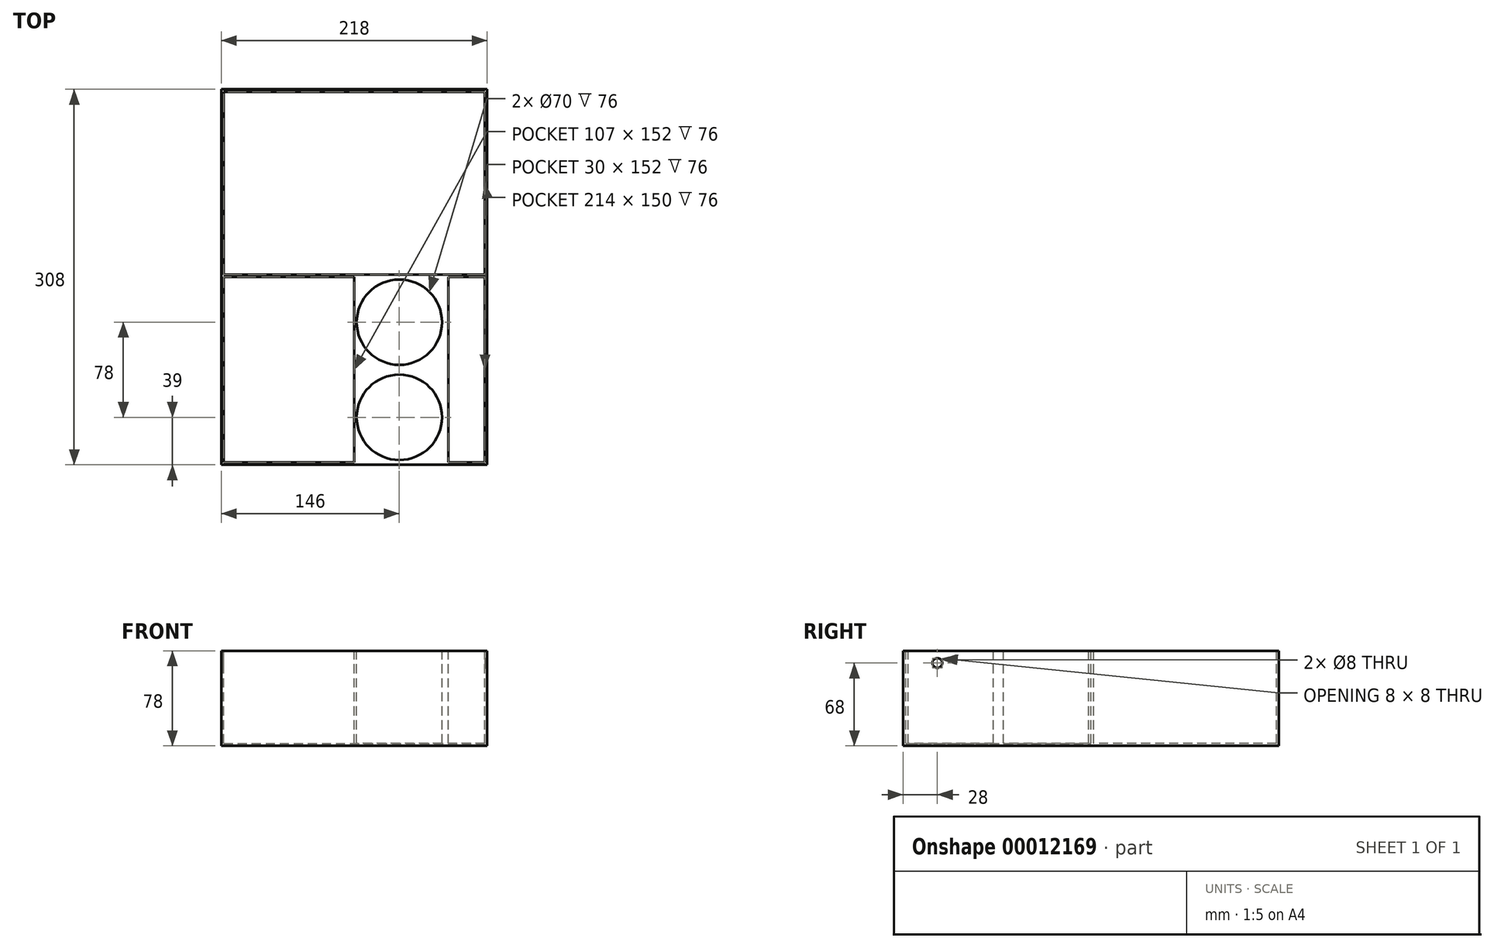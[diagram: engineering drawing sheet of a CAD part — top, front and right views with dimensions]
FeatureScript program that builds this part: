
annotation { "Feature Type Name" : "Feature", "Feature Type Description" : "" }
export const myFeature = defineFeature(function(context is Context, id is Id, definition is map)
    precondition{}
    {
        {
            var Q0;
            Q0=qCreatedBy(makeId("Top.planeOp"),FACE);
            var sketch = newSketch(context, id + "F0", { "sketchPlane" : qUnion([Q0])});
            skLineSegment(sketch, "E0.rect.bottom", {"start": v(109, 154) * mm, "end": v(-109, 154) * mm});
            skLineSegment(sketch, "E0.rect.top", {"start": v(109, -154) * mm, "end": v(-109, -154) * mm});
            skLineSegment(sketch, "E0.rect.left", {"start": v(109, 154) * mm, "end": v(109, -154) * mm});
            skLineSegment(sketch, "E0.rect.right", {"start": v(-109, 154) * mm, "end": v(-109, -154) * mm});
            skPoint(sketch, "E0.rect.middle", {"position": v(0, 0) * mm});
            skSolve(sketch);
        }
        {
            var Q0;
            Q0=makeQuery(id+"F0.imprint","IMPRINT",FACE,{"disambiguationData":[TD([[makeQuery(id+"F0.imprint","IMPRINT",EDGE,{"derivedFrom":sQuery(id+"F0.wireOp",EDGE,"E0.rect.bottom")}),1.0]])]});
            extrude(context, id + "F1", {"entities" : qUnion([Q0]), "depth" : 78 * mm});
        }
        {
            var Q0;
            Q0=makeQuery(id+"F1.opExtrude","CAP_FACE",FACE,{"disambiguationData":[OSD([sQuery(id+"F0.wireOp",EDGE,"E0.rect.bottom"),sQuery(id+"F0.wireOp",EDGE,"E0.rect.top"),sQuery(id+"F0.wireOp",EDGE,"E0.rect.left"),sQuery(id+"F0.wireOp",EDGE,"E0.rect.right")])],"isStart":false});
            var sketch = newSketch(context, id + "F2", { "sketchPlane" : qUnion([Q0])});
            skLineSegment(sketch, "E1", {"start": v(-109, 154) * mm, "end": v(-109, 152) * mm});
            skLineSegment(sketch, "E2", {"start": v(-109, 152) * mm, "end": v(-107, 152) * mm});
            skLineSegment(sketch, "E3", {"start": v(109, 154) * mm, "end": v(107, 154) * mm});
            skLineSegment(sketch, "E4", {"start": v(107, 154) * mm, "end": v(107, 152) * mm});
            skLineSegment(sketch, "E5.bottom", {"start": v(-107, 152) * mm, "end": v(107, 152) * mm});
            skLineSegment(sketch, "E5.top", {"start": v(-107, 2) * mm, "end": v(107, 2) * mm});
            skLineSegment(sketch, "E5.left", {"start": v(-107, 152) * mm, "end": v(-107, 2) * mm});
            skLineSegment(sketch, "E5.right", {"start": v(107, 152) * mm, "end": v(107, 2) * mm});
            skLineSegment(sketch, "E6", {"start": v(-107, 2) * mm, "end": v(-107, 0) * mm, "construction": true});
            skLineSegment(sketch, "E7", {"start": v(-109, -154) * mm, "end": v(-107, -154) * mm, "construction": true});
            skLineSegment(sketch, "E8", {"start": v(-107, -154) * mm, "end": v(-107, -152) * mm, "construction": true});
            skLineSegment(sketch, "E9.bottom", {"start": v(-107, -152) * mm, "end": v(0, -152) * mm});
            skLineSegment(sketch, "E9.top", {"start": v(-107, 0) * mm, "end": v(0, 0) * mm});
            skLineSegment(sketch, "E9.left", {"start": v(-107, -152) * mm, "end": v(-107, 0) * mm});
            skLineSegment(sketch, "E9.right", {"start": v(0, -152) * mm, "end": v(0, 0) * mm});
            skLineSegment(sketch, "E10", {"start": v(107, 2) * mm, "end": v(107, -154) * mm, "construction": true});
            skLineSegment(sketch, "E11", {"start": v(107, -154) * mm, "end": v(0, -154) * mm, "construction": true});
            skCircle(sketch, "E12", {"center": v(37, -115) * mm, "radius": 35 * mm});
            skCircle(sketch, "E13", {"center": v(37, -37) * mm, "radius": 35 * mm});
            skLineSegment(sketch, "E14", {"start": v(0, -37) * mm, "end": v(37, -37) * mm});
            skLineSegment(sketch, "E15", {"start": v(0, -115) * mm, "end": v(37, -115) * mm});
            skLineSegment(sketch, "E16.bottom", {"start": v(107, 0) * mm, "end": v(77, 0) * mm});
            skLineSegment(sketch, "E16.top", {"start": v(107, -152) * mm, "end": v(77, -152) * mm});
            skLineSegment(sketch, "E16.left", {"start": v(107, 0) * mm, "end": v(107, -152) * mm});
            skLineSegment(sketch, "E16.right", {"start": v(77, 0) * mm, "end": v(77, -152) * mm});
            skSolve(sketch);
        }
        {
            var Q0;
            Q0=makeQuery(id+"F2.imprint","IMPRINT",FACE,{"disambiguationData":[TD([[makeQuery(id+"F2.imprint","IMPRINT",EDGE,{"derivedFrom":sQuery(id+"F2.wireOp",EDGE,"E5.bottom")}),-1.0]])]});
            var Q1;
            Q1=makeQuery(id+"F2.imprint","IMPRINT",FACE,{"disambiguationData":[TD([[makeQuery(id+"F2.imprint","IMPRINT",EDGE,{"derivedFrom":sQuery(id+"F2.wireOp",EDGE,"E9.bottom")}),1.0]])]});
            var Q2;
            Q2=makeQuery(id+"F2.imprint","IMPRINT",FACE,{"disambiguationData":[TD([[makeQuery(id+"F2.imprint","IMPRINT",EDGE,{"derivedFrom":sQuery(id+"F2.wireOp",EDGE,"E13")}),1.0]])]});
            var Q3;
            Q3=makeQuery(id+"F2.imprint","IMPRINT",FACE,{"disambiguationData":[TD([[makeQuery(id+"F2.imprint","IMPRINT",EDGE,{"derivedFrom":sQuery(id+"F2.wireOp",EDGE,"E12")}),1.0]])]});
            var Q4;
            Q4=makeQuery(id+"F2.imprint","IMPRINT",FACE,{"disambiguationData":[TD([[makeQuery(id+"F2.imprint","IMPRINT",EDGE,{"derivedFrom":sQuery(id+"F2.wireOp",EDGE,"E16.bottom")}),1.0]])]});
            extrude(context, id + "F3", {"entities" : qUnion([Q0, Q1, Q2, Q3, Q4]), "operationType" : NewBodyOperationType.REMOVE, "oppositeDirection" : true, "depth" : 76 * mm});
        }
        {
            var Q0;
            Q0=makeQuery(id+"F1.opExtrude","SWEPT_FACE",FACE,{"disambiguationData":[OSD([sQuery(id+"F0.wireOp",EDGE,"E0.rect.left")])]});
            var sketch = newSketch(context, id + "F4", { "sketchPlane" : qUnion([Q0])});
            skCircle(sketch, "E17", {"center": v(-126, 68) * mm, "radius": 4 * mm});
            skSolve(sketch);
        }
        {
            var Q0;
            Q0 = qSketchRegion(id + "F4", true);
            extrude(context, id + "F5", {"entities" : qUnion([Q0]), "operationType" : NewBodyOperationType.REMOVE, "oppositeDirection" : true, "depth" : 4 * mm});
        }
        {
            var Q0;
            Q0=makeQuery(id+"F1.opExtrude","SWEPT_FACE",FACE,{"disambiguationData":[OSD([sQuery(id+"F0.wireOp",EDGE,"E0.rect.right")])]});
            var sketch = newSketch(context, id + "F6", { "sketchPlane" : qUnion([Q0])});
            skCircle(sketch, "E18", {"center": v(126, 68) * mm, "radius": 4 * mm});
            skSolve(sketch);
        }
        {
            var Q0;
            Q0 = qSketchRegion(id + "F6", true);
            extrude(context, id + "F7", {"entities" : qUnion([Q0]), "operationType" : NewBodyOperationType.REMOVE, "oppositeDirection" : true, "depth" : 3 * mm});
        }
    });
